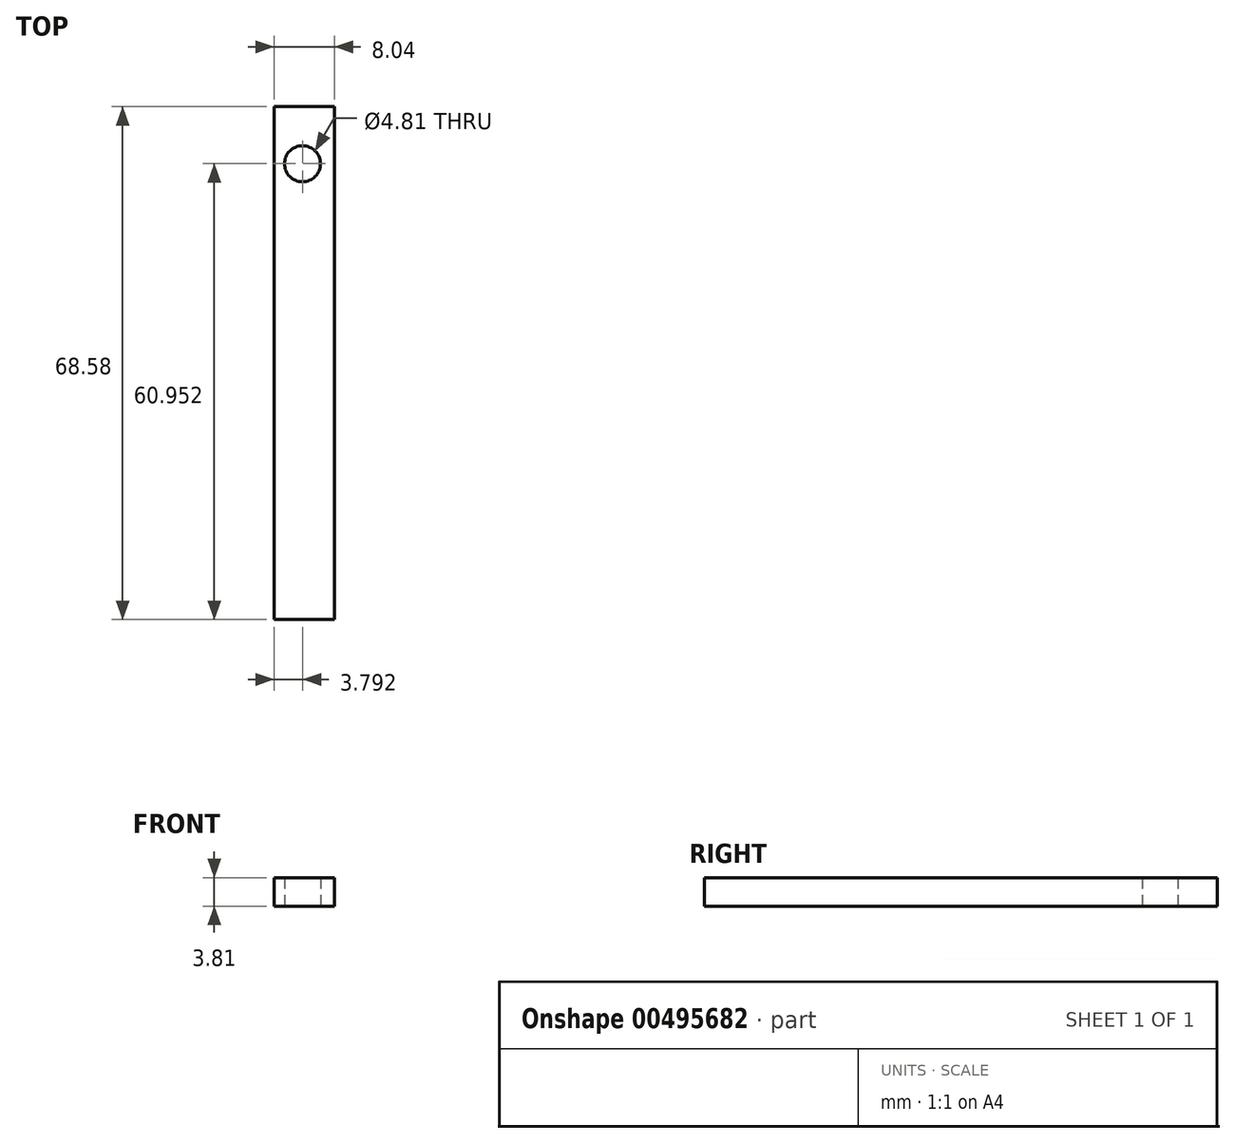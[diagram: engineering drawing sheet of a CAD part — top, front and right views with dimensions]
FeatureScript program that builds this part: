
annotation { "Feature Type Name" : "Feature", "Feature Type Description" : "" }
export const myFeature = defineFeature(function(context is Context, id is Id, definition is map)
    precondition{}
    {
        {
            var Q0;
            Q0=qCreatedBy(makeId("Top.planeOp"),FACE);
            var sketch = newSketch(context, id + "F0", { "sketchPlane" : qUnion([Q0])});
            skLineSegment(sketch, "E0", {"start": v(-8.04, 12.28) * mm, "end": v(-8.04, -56.3) * mm});
            skLineSegment(sketch, "E1", {"start": v(-8.04, -56.3) * mm, "end": v(0, -56.3) * mm});
            skLineSegment(sketch, "E2", {"start": v(0, -56.3) * mm, "end": v(0, 12.28) * mm});
            skLineSegment(sketch, "E3", {"start": v(0, 12.28) * mm, "end": v(-8.04, 12.28) * mm});
            skCircle(sketch, "E4", {"center": v(-4.25, 4.65) * mm, "radius": 2.4 * mm});
            skCircle(sketch, "E5", {"center": v(-4.25, 4.65) * mm, "radius": 2.02 * mm});
            skSolve(sketch);
        }
        {
            var Q0;
            Q0 = qSketchRegion(id + "F0", true);
            extrude(context, id + "F1", {"entities" : qUnion([Q0]), "depth" : 3.8 * mm});
        }
    });
